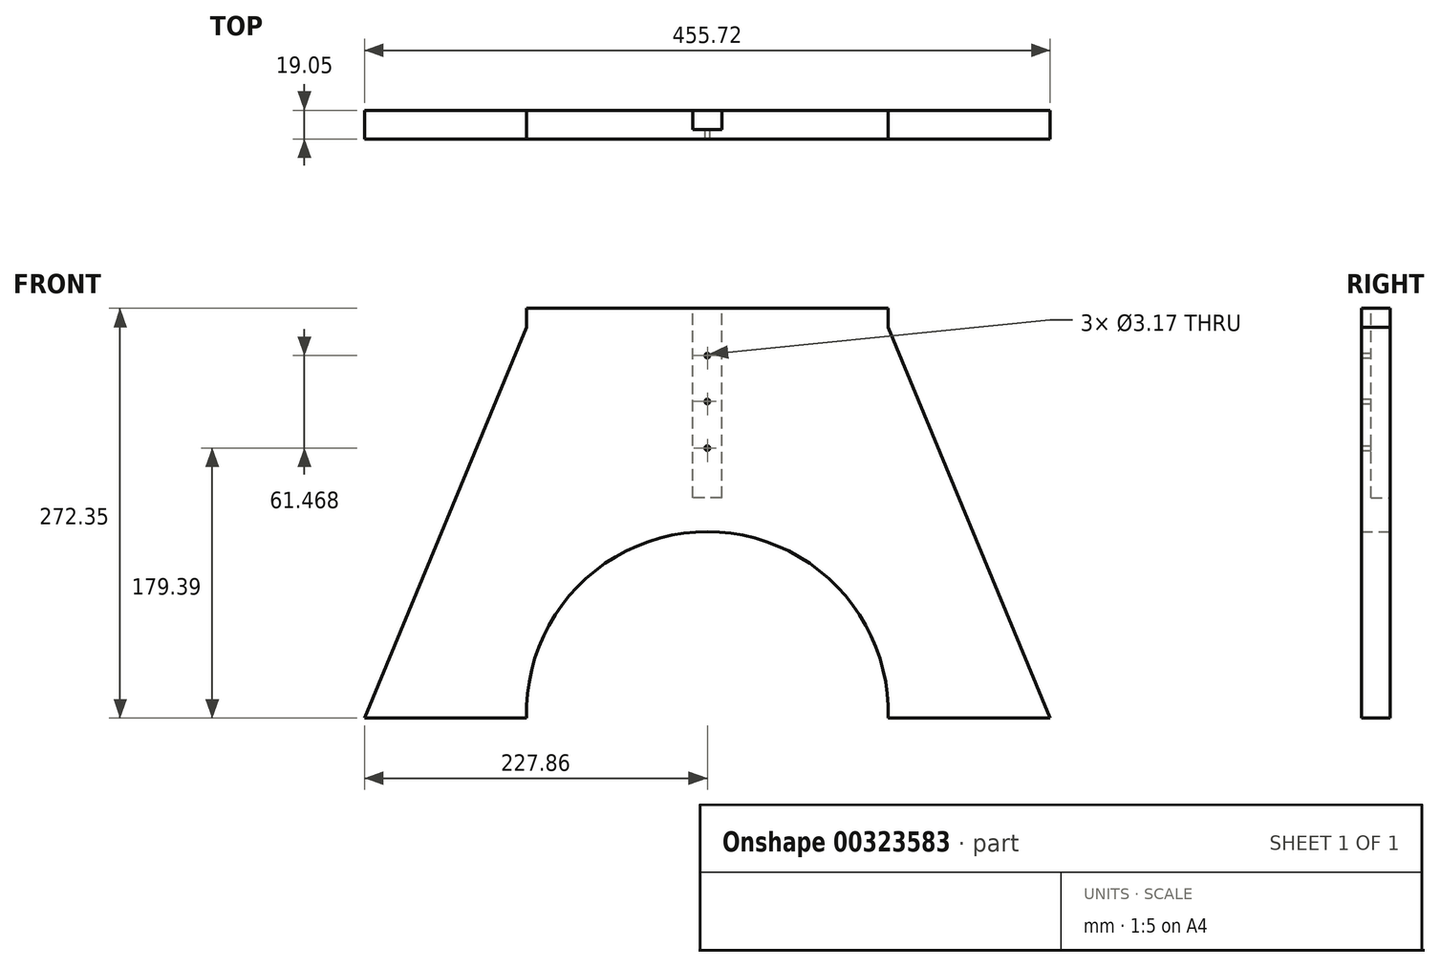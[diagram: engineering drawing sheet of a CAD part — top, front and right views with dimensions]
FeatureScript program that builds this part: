
annotation { "Feature Type Name" : "Feature", "Feature Type Description" : "" }
export const myFeature = defineFeature(function(context is Context, id is Id, definition is map)
    precondition{}
    {
        {
            var Q0;
            Q0=qCreatedBy(makeId("Front.planeOp"),FACE);
            var sketch = newSketch(context, id + "F0", { "sketchPlane" : qUnion([Q0])});
            skLineSegment(sketch, "E0", {"start": v(0, 155.77) * mm, "end": v(120.14, 155.77) * mm});
            skLineSegment(sketch, "E1", {"start": v(0, 155.77) * mm, "end": v(-120.14, 155.77) * mm});
            skLineSegment(sketch, "E2", {"start": v(227.86, -116.58) * mm, "end": v(120.14, -116.58) * mm});
            skLineSegment(sketch, "E3", {"start": v(0, 155.77) * mm, "end": v(0, 7.25) * mm, "construction": true});
            skLineSegment(sketch, "E4.MirrorCS", {"start": v(-227.86, -116.58) * mm, "end": v(-120.14, -116.58) * mm});
            skArc(sketch, "E5", {"start": v(120.14, -116.58) * mm, "mid": v(0, 7.25) * mm, "end": v(-120.14, -116.58) * mm});
            skPoint(sketch, "E5.third.point", {"position": v(-120.14, -109.32) * mm});
            skLineSegment(sketch, "E6.trimOffspring", {"start": v(0, -112.95) * mm, "end": v(0, -115.14) * mm, "construction": true});
            skLineSegment(sketch, "E7", {"start": v(120.14, 155.77) * mm, "end": v(120.14, 143.07) * mm});
            skLineSegment(sketch, "E8", {"start": v(120.14, 143.07) * mm, "end": v(227.86, -116.58) * mm});
            skLineSegment(sketch, "E9", {"start": v(-120.14, 155.77) * mm, "end": v(-120.14, 143.07) * mm});
            skLineSegment(sketch, "E10", {"start": v(-120.14, 143.07) * mm, "end": v(-227.86, -116.58) * mm});
            skSolve(sketch);
        }
        {
            var Q0;
            Q0=qSketchRegion(id+"F0",true);
            extrude(context, id + "F1", {"entities" : qUnion([Q0]), "depth" : 19.05 * mm});
        }
        {
            var Q0;
            Q0=qCreatedBy(makeId("Front.planeOp"),FACE);
            var sketch = newSketch(context, id + "F2", { "sketchPlane" : qUnion([Q0])});
            skLineSegment(sketch, "E11", {"start": v(0, 0) * mm, "end": v(0, 29.8) * mm, "construction": true});
            skLineSegment(sketch, "E12", {"start": v(0, 29.8) * mm, "end": v(-9.65, 29.8) * mm});
            skPoint(sketch, "E13.orphan", {"position": v(0, 62.81) * mm});
            skLineSegment(sketch, "E14", {"start": v(0, 29.8) * mm, "end": v(0, 157.41) * mm, "construction": true});
            skLineSegment(sketch, "E15.MirrorCS", {"start": v(0, 29.8) * mm, "end": v(9.65, 29.8) * mm});
            skLineSegment(sketch, "E16", {"start": v(9.65, 29.8) * mm, "end": v(9.65, 155.77) * mm});
            skLineSegment(sketch, "E17", {"start": v(9.65, 155.77) * mm, "end": v(0, 155.77) * mm});
            skLineSegment(sketch, "E18.MirrorCS", {"start": v(-9.65, 29.8) * mm, "end": v(-9.65, 155.77) * mm});
            skLineSegment(sketch, "E19.MirrorCS", {"start": v(-9.65, 155.77) * mm, "end": v(0, 155.77) * mm});
            skCircle(sketch, "E20", {"center": v(0, 124.28) * mm, "radius": 1.59 * mm});
            skCircle(sketch, "E21", {"center": v(0, 93.8) * mm, "radius": 1.59 * mm});
            skCircle(sketch, "E22", {"center": v(0, 62.81) * mm, "radius": 1.59 * mm});
            skSolve(sketch);
        }
        {
            var Q0;
            Q0=qSketchRegion(id+"F2",true);
            extrude(context, id + "F3", {"entities" : qUnion([Q0]), "operationType" : NewBodyOperationType.REMOVE, "depth" : 12.7 * mm});
        }
        {
            var Q0;
            Q0=makeQuery(id+"F3.boolean.opBoolean","SPLIT",FACE,{"disambiguationData":[TD([makeQuery(id+"F3.opExtrude","SWEPT_FACE",FACE,{"disambiguationData":[OSD([sQuery(id+"F2.wireOp",EDGE,"E20")])]})])],"derivedFrom":makeQuery(id+"F1.opExtrude","CAP_FACE",FACE,{"disambiguationData":[OSD([sQuery(id+"F0.wireOp",EDGE,"E0"),sQuery(id+"F0.wireOp",EDGE,"E1"),sQuery(id+"F0.wireOp",EDGE,"E2"),sQuery(id+"F0.wireOp",EDGE,"E4.MirrorCS"),sQuery(id+"F0.wireOp",EDGE,"E5"),sQuery(id+"F0.wireOp",EDGE,"E7"),sQuery(id+"F0.wireOp",EDGE,"E8"),sQuery(id+"F0.wireOp",EDGE,"E9"),sQuery(id+"F0.wireOp",EDGE,"E10")])],"isStart":true})});
            var Q1;
            Q1=sQuery(id+"F2.wireOp",EDGE,"E20");
            extrude(context, id + "F4", {"entities" : qUnion([Q0]), "operationType" : NewBodyOperationType.REMOVE, "surfaceEntities" : qUnion([Q1]), "oppositeDirection" : true, "depth" : 19.05 * mm});
        }
        {
            var Q0;
            Q0=makeQuery(id+"F3.boolean.opBoolean","SPLIT",FACE,{"disambiguationData":[TD([makeQuery(id+"F3.opExtrude","SWEPT_FACE",FACE,{"disambiguationData":[OSD([sQuery(id+"F2.wireOp",EDGE,"E21")])]})])],"derivedFrom":makeQuery(id+"F1.opExtrude","CAP_FACE",FACE,{"disambiguationData":[OSD([sQuery(id+"F0.wireOp",EDGE,"E0"),sQuery(id+"F0.wireOp",EDGE,"E1"),sQuery(id+"F0.wireOp",EDGE,"E2"),sQuery(id+"F0.wireOp",EDGE,"E4.MirrorCS"),sQuery(id+"F0.wireOp",EDGE,"E5"),sQuery(id+"F0.wireOp",EDGE,"E7"),sQuery(id+"F0.wireOp",EDGE,"E8"),sQuery(id+"F0.wireOp",EDGE,"E9"),sQuery(id+"F0.wireOp",EDGE,"E10")])],"isStart":true})});
            var Q1;
            Q1=sQuery(id+"F2.wireOp",EDGE,"E21");
            extrude(context, id + "F5", {"entities" : qUnion([Q0]), "operationType" : NewBodyOperationType.REMOVE, "surfaceEntities" : qUnion([Q1]), "oppositeDirection" : true, "depth" : 19.05 * mm});
        }
        {
            var Q0;
            Q0=makeQuery(id+"F3.boolean.opBoolean","SPLIT",FACE,{"disambiguationData":[TD([makeQuery(id+"F3.opExtrude","SWEPT_FACE",FACE,{"disambiguationData":[OSD([sQuery(id+"F2.wireOp",EDGE,"E22")])]})])],"derivedFrom":makeQuery(id+"F1.opExtrude","CAP_FACE",FACE,{"disambiguationData":[OSD([sQuery(id+"F0.wireOp",EDGE,"E0"),sQuery(id+"F0.wireOp",EDGE,"E1"),sQuery(id+"F0.wireOp",EDGE,"E2"),sQuery(id+"F0.wireOp",EDGE,"E4.MirrorCS"),sQuery(id+"F0.wireOp",EDGE,"E5"),sQuery(id+"F0.wireOp",EDGE,"E7"),sQuery(id+"F0.wireOp",EDGE,"E8"),sQuery(id+"F0.wireOp",EDGE,"E9"),sQuery(id+"F0.wireOp",EDGE,"E10")])],"isStart":true})});
            var Q1;
            Q1=sQuery(id+"F2.wireOp",EDGE,"E22");
            extrude(context, id + "F6", {"entities" : qUnion([Q0]), "operationType" : NewBodyOperationType.REMOVE, "surfaceEntities" : qUnion([Q1]), "oppositeDirection" : true, "depth" : 19.05 * mm});
        }
    });
